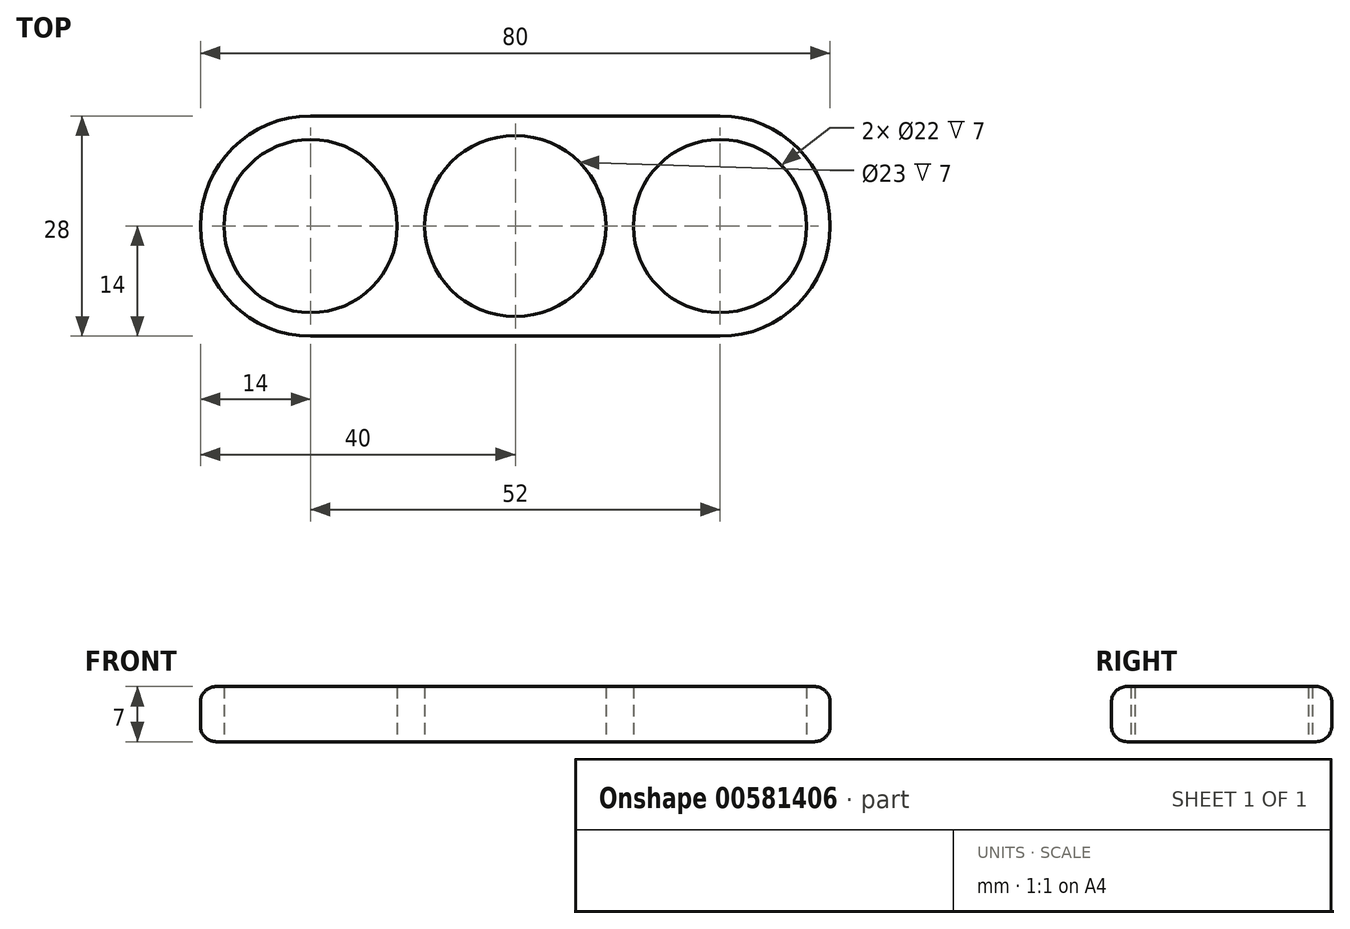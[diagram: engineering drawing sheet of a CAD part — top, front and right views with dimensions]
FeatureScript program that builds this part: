
annotation { "Feature Type Name" : "Feature", "Feature Type Description" : "" }
export const myFeature = defineFeature(function(context is Context, id is Id, definition is map)
    precondition{}
    {
        {
            var Q0;
            Q0=qCreatedBy(makeId("Top.planeOp"),FACE);
            var sketch = newSketch(context, id + "F0", { "sketchPlane" : qUnion([Q0])});
            skCircle(sketch, "E0", {"center": v(0, 0) * mm, "radius": 11.5 * mm});
            skLineSegment(sketch, "E1", {"start": v(0, 0) * mm, "end": v(26, 0) * mm});
            skCircle(sketch, "E2", {"center": v(26, 0) * mm, "radius": 11 * mm});
            skArc(sketch, "E3.0", {"start": v(26, -14) * mm, "mid": v(40, 0) * mm, "end": v(26, 14) * mm});
            skPoint(sketch, "E4.center", {"position": v(-3, 0) * mm});
            skCircle(sketch, "E5.1.0", {"center": v(-26, 0) * mm, "radius": 11 * mm});
            skArc(sketch, "E6.1.0", {"start": v(-26, 14) * mm, "mid": v(-40, 0) * mm, "end": v(-26, -14) * mm});
            skLineSegment(sketch, "E7", {"start": v(-26, 14) * mm, "end": v(26, 14) * mm});
            skLineSegment(sketch, "E8", {"start": v(-26, -14) * mm, "end": v(26, -14) * mm});
            skSolve(sketch);
        }
        {
            var Q0;
            Q0 = qSketchRegion(id + "F0", true);
            extrude(context, id + "F1", {"entities" : qUnion([Q0]), "depth" : 7 * mm, "offsetDistance" : 25 * mm});
        }
        {
            var Q0;
            Q0=makeQuery(id+"F1.opExtrude","CAP_EDGE",EDGE,{"disambiguationData":[OSD([sQuery(id+"F0.wireOp",EDGE,"E7")])],"isStart":false});
            var Q1;
            Q1=makeQuery(id+"F1.opExtrude","CAP_EDGE",EDGE,{"disambiguationData":[OSD([sQuery(id+"F0.wireOp",EDGE,"E3.0")])],"isStart":false});
            var Q2;
            Q2=makeQuery(id+"F1.opExtrude","CAP_EDGE",EDGE,{"disambiguationData":[OSD([sQuery(id+"F0.wireOp",EDGE,"E8")])],"isStart":false});
            var Q3;
            Q3=makeQuery(id+"F1.opExtrude","CAP_EDGE",EDGE,{"disambiguationData":[OSD([sQuery(id+"F0.wireOp",EDGE,"E6.1.0")])],"isStart":false});
            var Q4;
            Q4=makeQuery(id+"F1.opExtrude","CAP_EDGE",EDGE,{"disambiguationData":[OSD([sQuery(id+"F0.wireOp",EDGE,"E3.0")])],"isStart":true});
            var Q5;
            Q5=makeQuery(id+"F1.opExtrude","CAP_EDGE",EDGE,{"disambiguationData":[OSD([sQuery(id+"F0.wireOp",EDGE,"E7")])],"isStart":true});
            var Q6;
            Q6=makeQuery(id+"F1.opExtrude","CAP_EDGE",EDGE,{"disambiguationData":[OSD([sQuery(id+"F0.wireOp",EDGE,"E6.1.0")])],"isStart":true});
            var Q7;
            Q7=makeQuery(id+"F1.opExtrude","CAP_EDGE",EDGE,{"disambiguationData":[OSD([sQuery(id+"F0.wireOp",EDGE,"E8")])],"isStart":true});
            fillet(context, id + "F2", {"entities" : qUnion([Q0, Q1, Q2, Q3, Q4, Q5, Q6, Q7]), "radius" : 2 * mm, "tangentPropagation" : true, "allowEdgeOverflow" : false});
        }
    });
